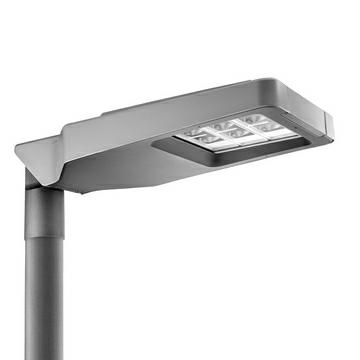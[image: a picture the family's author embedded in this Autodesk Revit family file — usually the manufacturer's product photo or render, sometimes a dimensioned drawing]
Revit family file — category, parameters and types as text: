
# Revit family: Lighting-Stradale-GEWISS-ROAD[5]MINI-LED_OTTICA_WIDE_CLII
name_source: partatom
category: Apparecchi per illuminazione
units: mm (PartAtom-declared; Revit-internal decimal feet)

## family parameters
Basato su piano di lavoro = No
Condiviso = No
Punto di calcolo locali = No
Quota connettore circolare = Usa diametro
Sempre verticale = Sì
Sorgente d'illuminazione = No
Taglio con vuoti quando caricato = No
Tipo di parte = Normale

## types (1)
- Lighting-Stradale-GEWISS-ROAD[5]MINI-LED_OTTICA_WIDE_CLII
    Alimentatore = Incluso
    Apparecchio a ridotta temperatura superficiale = -
    Applicazione = Esterno
    Cablaggio = Sezionatore
    Caratteristiche elettriche e gestione della luce = -
    Caratteristiche ottiche e illuminotecniche = -
    Carico apparente = 53 VA
    Catalogo = LIGHTING
    Catalogo Serie = ROAD [5]
    Certificazione DIN 18032-3 = -
    Certificazioni e classificazioni = -
    Classe fotobiologica = RG0
    Classe isolamento = II
    Classificazione: = -
    Codice Electrocod = 244C
    Codice digitale univoco (Datamatrix) = Attualmente non presente
    Colore = Grigio grafite
    Commenti sul wattaggio = 53W
    Contesto = Illuminazione stradale e parcheggi
    Controllo abbagliamento e luminanza = G*3 - ULOR = 0
    Corpo = Alluminio pressofuso
    Corrente di pilotaggio. = 0,7A
    Descrizione = GWR5272V - ROAD5 MINI V.WIDE 2M 4000K 0,7A CL2
    Dispositivo di protezione = DM 10KV / CM 10KV
    Distanza minima dall'oggetto illuminato = 1M
    Durata di vita = L90B10 (Tq+25°C) = 100.000 h - L90B10 (Tq+50°C) = 75.000 h
    Efficienza luminosa (lm/W) = 119
    Finitura colore = Verniciato a polveri
    Fissaggio = Testa palo - Sbraccio
    Flusso nominale (lm) = 6240
    Frequenza nominale (Hz) = 50 / 60
    Gancio di chiusura = Maniglia frontale integrata
    Garanzia = 5 anni
    Grado di protezione = IP66
    Gruppo ottico = Riflettore in PC metallizzato
    Guarnizioni = silicone antinvecchiamento
    IDF = 4d70a5c1-4650-4971-bd14-1db705aa8851
    IDT = 3cb2f9b43b7a40689a44ddfc6caf9e96
    IPEA = STRADALE = A5+ // GRANDI AREE = A5+ // CICLOPEDONALI = A4+ // AREE VERDI = A4+ // CENTRO STORICO = A6+
    Immagine tipo = GWR5276M.jpg
    Inclinazione = -20° ÷ +10° sbraccio - -10° ÷ +20° testa palo
    Indice di resa cromatica = CRI-70
    Informazioni generali = -
    Installazione e manutenzione = -
    LED Life Time (L80B05) = 77000H
    Lampada: = LED
    Lumen output (lm) = 6400
    Materiali = -
    Modello = GWR5272V
    Norma di riferimento = EN 60598-2-3, EN 60598-1 IEC/TR 62778
    Numero moduli = 2 (2x3 LED)
    Ottica = WIDE
    Peso (kg): = 6,6
    Potenza assorbita : = 54 W @ 0.7A
    Potenza di sistema = 53W
    Produttore = GEWISS S.p.A.
    Regolazione inclinazione = -20° ÷ +10° sbraccio - -10° ÷ +20° testa palo
    Resistenza agli urti = IK08
    Resistenza al filo incandescente = -
    SEO = Stradale
    Scheda Tecnica = https://www.gewiss.com
    Schermo = Vetro piano temperato spessore 4mm
    Sistema di controllo = DALI - 5 Step
    Sostituibilità gruppo ottico = Non disponibile
    Sostituibilità piastra di cablaggio = Non disponibile
    Superficie massima esposta al vento = 0,149999999999999M2
    Superficie massima esposta al vento : = 0,15 m²
    Temperatura di colore = 4000K
    Temperatura di colore: = 4000 K (CRI>70)
    Temperatura di esercizio = -25 +50 °C
    Temperatura di stoccaggio = -
    Temperatura di utilizzo = -25 +40 °C
    Tensione = 220/240 V - 50/60 Hz - Stand alone e/o Programmabile
    Tensione di alimentazione = 220 - 240 V
    Tipo di apparecchio = Apparecchiatura stradale a LED
    Tipo di installazione e montaggio = Testa palo - Sbraccio
    Tipologia = Programmabile (5 passi)
    Tipologia sorgente luminosa = LED - Non sostituibile
    Tolleranza cromatica = SDCM = 5
    URL = https://www.gewiss.com
    Vano di alimentazione = Integrato
    Versione file RFA = 20.11
    Viti esterne = Acciaio inox
